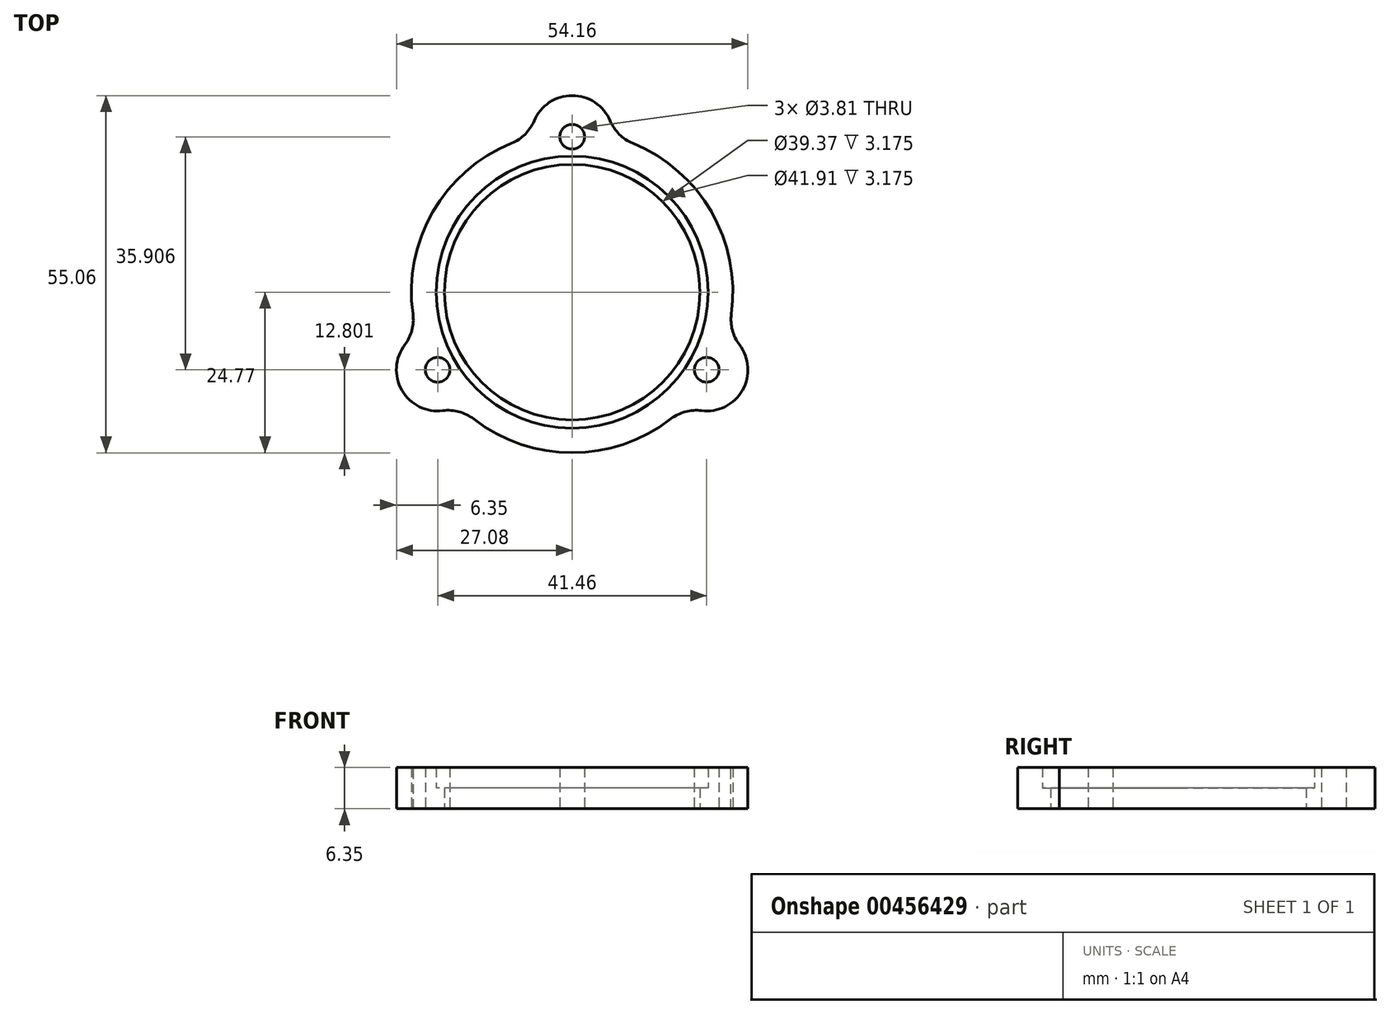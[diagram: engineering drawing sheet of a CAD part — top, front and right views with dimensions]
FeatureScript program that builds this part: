
annotation { "Feature Type Name" : "Feature", "Feature Type Description" : "" }
export const myFeature = defineFeature(function(context is Context, id is Id, definition is map)
    precondition{}
    {
        {
            var Q0;
            Q0=qCreatedBy(makeId("Top.planeOp"),FACE);
            var sketch = newSketch(context, id + "F0", { "sketchPlane" : qUnion([Q0])});
            skCircle(sketch, "E0", {"center": v(0, 0) * mm, "radius": 20.96 * mm});
            skCircle(sketch, "E1", {"center": v(0, 0) * mm, "radius": 19.69 * mm});
            skCircle(sketch, "E2", {"center": v(0, 0) * mm, "radius": 24.77 * mm});
            skLineSegment(sketch, "E3", {"start": v(0, 0) * mm, "end": v(0, 42.77) * mm, "construction": true});
            skLineSegment(sketch, "E4", {"start": v(0, 0) * mm, "end": v(-43.71, -25.24) * mm, "construction": true});
            skLineSegment(sketch, "E5", {"start": v(0, 0) * mm, "end": v(46.9, -27.08) * mm, "construction": true});
            skLineSegment(sketch, "E6", {"start": v(-6.35, 2.16) * mm, "end": v(-6.35, 48.97) * mm, "construction": true});
            skLineSegment(sketch, "E7.MirrorCS", {"start": v(6.35, 2.16) * mm, "end": v(6.35, 48.97) * mm, "construction": true});
            skLineSegment(sketch, "E8", {"start": v(-11.23, 0.85) * mm, "end": v(-48.99, -20.95) * mm, "construction": true});
            skLineSegment(sketch, "E9.MirrorCS", {"start": v(-4.88, -10.15) * mm, "end": v(-42.64, -31.95) * mm, "construction": true});
            skLineSegment(sketch, "E10", {"start": v(0.14, -7.41) * mm, "end": v(38.48, -29.55) * mm, "construction": true});
            skLineSegment(sketch, "E11.MirrorCS", {"start": v(6.49, 3.59) * mm, "end": v(44.83, -18.55) * mm, "construction": true});
            skArc(sketch, "E12", {"start": v(6.35, 23.94) * mm, "mid": v(0, 30.29) * mm, "end": v(-6.35, 23.94) * mm});
            skArc(sketch, "E13", {"start": v(-23.9, -6.47) * mm, "mid": v(-26.23, -15.14) * mm, "end": v(-17.56, -17.47) * mm});
            skArc(sketch, "E14", {"start": v(17.56, -17.47) * mm, "mid": v(26.23, -15.14) * mm, "end": v(23.9, -6.47) * mm});
            skCircle(sketch, "E15", {"center": v(0, 23.94) * mm, "radius": 1.9 * mm});
            skCircle(sketch, "E16", {"center": v(-20.73, -11.97) * mm, "radius": 1.9 * mm});
            skCircle(sketch, "E17", {"center": v(20.73, -11.97) * mm, "radius": 1.9 * mm});
            skSolve(sketch);
        }
        {
            var Q0;
            Q0=makeQuery(id+"F0.imprint","IMPRINT",FACE,{"disambiguationData":[TD([[makeQuery(id+"F0.imprint","IMPRINT",EDGE,{"derivedFrom":sQuery(id+"F0.wireOp",EDGE,"E0")}),1.0]])]});
            extrude(context, id + "F1", {"entities" : qUnion([Q0]), "depth" : 3.17 * mm});
        }
        {
            var Q0;
            Q0 = qSketchRegion(id + "F0", true);
            extrude(context, id + "F2", {"entities" : qUnion([Q0]), "operationType" : NewBodyOperationType.ADD, "depth" : 6.35 * mm});
        }
        {
            var Q0;
            {var subQ0=sQuery(id+"F0.wireOp",EDGE,"E12");var subQ1=sQuery(id+"F0.wireOp",EDGE,"E2");Q0=makeQuery(id+"F2.opExtrude","SWEPT_EDGE",EDGE,{"disambiguationData":[OSD([subQ1,subQ0]),TDD([makeQuery(id+"F0.imprint","INTERSECT",VERTEX,{"disambiguationData":[OD(0.0)],"derivedFrom":[subQ1,subQ0]})])]});}
            var Q1;
            {var subQ0=sQuery(id+"F0.wireOp",EDGE,"E12");var subQ1=sQuery(id+"F0.wireOp",EDGE,"E2");Q1=makeQuery(id+"F2.opExtrude","SWEPT_EDGE",EDGE,{"disambiguationData":[OSD([subQ1,subQ0]),TDD([makeQuery(id+"F0.imprint","INTERSECT",VERTEX,{"disambiguationData":[OD(1.0)],"derivedFrom":[subQ1,subQ0]})])]});}
            var Q2;
            {var subQ0=sQuery(id+"F0.wireOp",EDGE,"E13");var subQ1=sQuery(id+"F0.wireOp",EDGE,"E2");Q2=makeQuery(id+"F2.opExtrude","SWEPT_EDGE",EDGE,{"disambiguationData":[OSD([subQ1,subQ0]),TDD([makeQuery(id+"F0.imprint","INTERSECT",VERTEX,{"disambiguationData":[OD(0.0)],"derivedFrom":[subQ1,subQ0]})])]});}
            var Q3;
            {var subQ0=sQuery(id+"F0.wireOp",EDGE,"E13");var subQ1=sQuery(id+"F0.wireOp",EDGE,"E2");Q3=makeQuery(id+"F2.opExtrude","SWEPT_EDGE",EDGE,{"disambiguationData":[OSD([subQ1,subQ0]),TDD([makeQuery(id+"F0.imprint","INTERSECT",VERTEX,{"disambiguationData":[OD(1.0)],"derivedFrom":[subQ1,subQ0]})])]});}
            var Q4;
            {var subQ0=sQuery(id+"F0.wireOp",EDGE,"E14");var subQ1=sQuery(id+"F0.wireOp",EDGE,"E2");Q4=makeQuery(id+"F2.opExtrude","SWEPT_EDGE",EDGE,{"disambiguationData":[OSD([subQ1,subQ0]),TDD([makeQuery(id+"F0.imprint","INTERSECT",VERTEX,{"disambiguationData":[OD(1.0)],"derivedFrom":[subQ1,subQ0]})])]});}
            var Q5;
            {var subQ0=sQuery(id+"F0.wireOp",EDGE,"E14");var subQ1=sQuery(id+"F0.wireOp",EDGE,"E2");Q5=makeQuery(id+"F2.opExtrude","SWEPT_EDGE",EDGE,{"disambiguationData":[OSD([subQ1,subQ0]),TDD([makeQuery(id+"F0.imprint","INTERSECT",VERTEX,{"disambiguationData":[OD(0.0)],"derivedFrom":[subQ1,subQ0]})])]});}
            fillet(context, id + "F3", {"entities" : qUnion([Q0, Q1, Q2, Q3, Q4, Q5]), "radius" : 6.35 * mm, "tangentPropagation" : true, "allowEdgeOverflow" : false});
        }
    });
